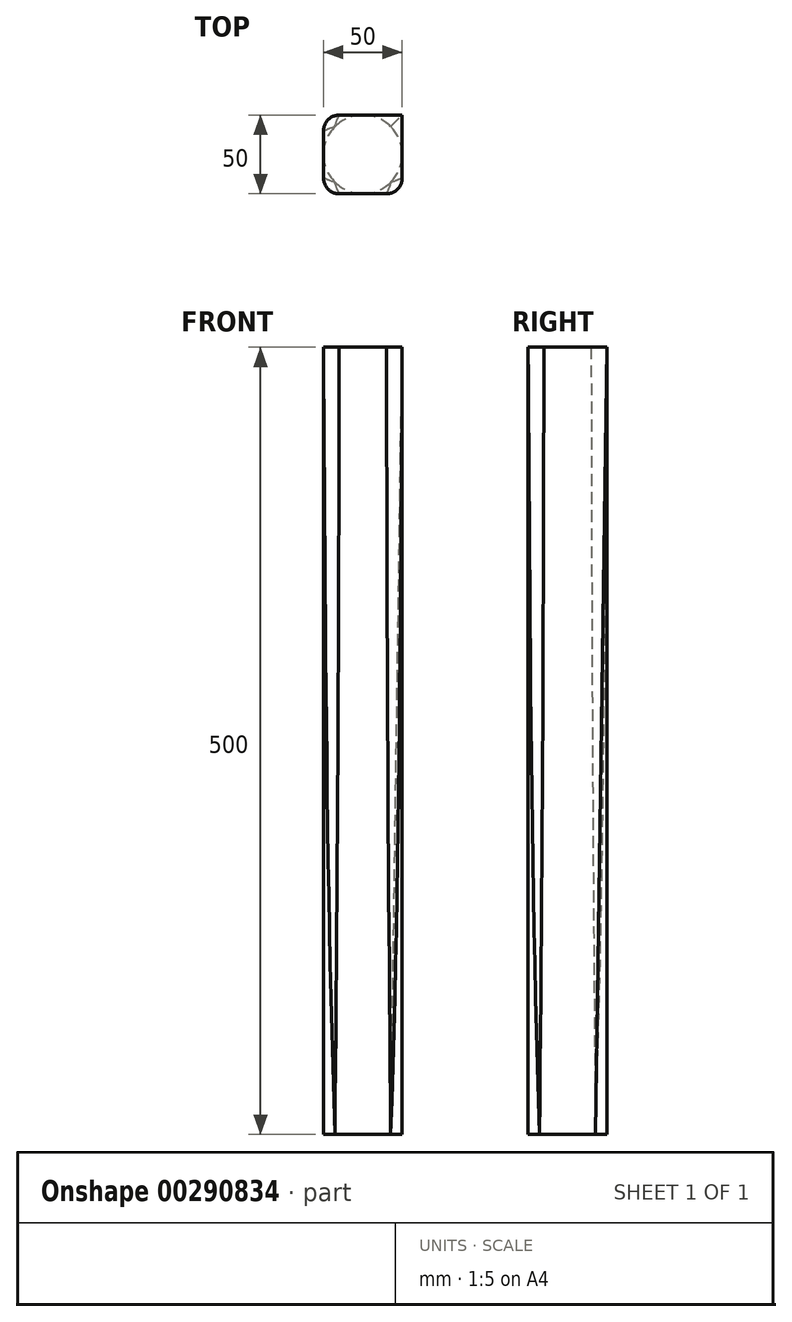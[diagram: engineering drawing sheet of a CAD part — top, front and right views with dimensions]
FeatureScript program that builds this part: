
annotation { "Feature Type Name" : "Feature", "Feature Type Description" : "" }
export const myFeature = defineFeature(function(context is Context, id is Id, definition is map)
    precondition{}
    {
        {
            var Q0;
            Q0=qCreatedBy(makeId("Top.planeOp"),FACE);
            var sketch = newSketch(context, id + "F0", { "sketchPlane" : qUnion([Q0])});
            skCircle(sketch, "E0", {"center": v(0, 0) * mm, "radius": 25 * mm});
            skSolve(sketch);
        }
        {
            var Q0;
            Q0=qCreatedBy(makeId("Top.planeOp"),FACE);
            cPlane(context, id + "F1", {"entities" : qUnion([Q0]), "cplaneType" : CPlaneType.OFFSET, "offset" : 500 * mm, "width" : 150 * mm, "height" : 150 * mm});
        }
        {
            var Q0;
            Q0=qCreatedBy(id+"F1.planeOp",FACE);
            var sketch = newSketch(context, id + "F2", { "sketchPlane" : qUnion([Q0])});
            skLineSegment(sketch, "E1.bottom", {"start": v(25, -25) * mm, "end": v(-25, -25) * mm});
            skLineSegment(sketch, "E1.top", {"start": v(25, 25) * mm, "end": v(-25, 25) * mm});
            skLineSegment(sketch, "E1.left", {"start": v(25, -25) * mm, "end": v(25, 25) * mm});
            skLineSegment(sketch, "E1.right", {"start": v(-25, -25) * mm, "end": v(-25, 25) * mm});
            skPoint(sketch, "E1.middle", {"position": v(0, 0) * mm});
            skSolve(sketch);
        }
        {
            var Q0;
            Q0=makeQuery(id+"F0.imprint","IMPRINT",FACE,{"disambiguationData":[TD([[makeQuery(id+"F0.imprint","IMPRINT",EDGE,{"derivedFrom":sQuery(id+"F0.wireOp",EDGE,"E0")}),1.0]])]});
            var Q1;
            Q1=makeQuery(id+"F2.imprint","IMPRINT",FACE,{"disambiguationData":[TD([[makeQuery(id+"F2.imprint","IMPRINT",EDGE,{"derivedFrom":sQuery(id+"F2.wireOp",EDGE,"E1.bottom")}),-1.0]])]});
            loft(context, id + "F3", {"sheetProfilesArray" : [{ "sheetProfileEntities" : qUnion([Q0]) }, { "sheetProfileEntities" : qUnion([Q1]) }]});
        }
        {
            var Q0;
            Q0=makeQuery(id+"F3.opLoft","SWEPT_EDGE",EDGE,{"disambiguationData":[OSD([sQuery(id+"F2.wireOp",EDGE,"E1.bottom"),sQuery(id+"F2.wireOp",EDGE,"E1.left")])]});
            var Q1;
            Q1=makeQuery(id+"F3.opLoft","SWEPT_EDGE",EDGE,{"disambiguationData":[OSD([sQuery(id+"F0.wireOp",EDGE,"E0"),sQuery(id+"F2.wireOp",EDGE,"E1.bottom"),sQuery(id+"F2.wireOp",EDGE,"E1.top"),sQuery(id+"F2.wireOp",EDGE,"E1.right")])]});
            var Q2;
            Q2=makeQuery(id+"F3.opLoft","SWEPT_EDGE",EDGE,{"disambiguationData":[OSD([sQuery(id+"F0.wireOp",EDGE,"E0"),sQuery(id+"F2.wireOp",EDGE,"E1.top"),sQuery(id+"F2.wireOp",EDGE,"E1.left"),sQuery(id+"F2.wireOp",EDGE,"E1.right")])]});
            var Q3;
            Q3=makeQuery(id+"F3.opLoft","SWEPT_EDGE",EDGE,{"disambiguationData":[OSD([sQuery(id+"F0.wireOp",EDGE,"E0"),sQuery(id+"F2.wireOp",EDGE,"E1.bottom"),sQuery(id+"F2.wireOp",EDGE,"E1.top"),sQuery(id+"F2.wireOp",EDGE,"E1.left")])]});
            fillet(context, id + "F4", {"entities" : qUnion([Q0, Q1, Q2, Q3]), "radius" : 10 * mm, "tangentPropagation" : true, "allowEdgeOverflow" : false});
        }
    });
